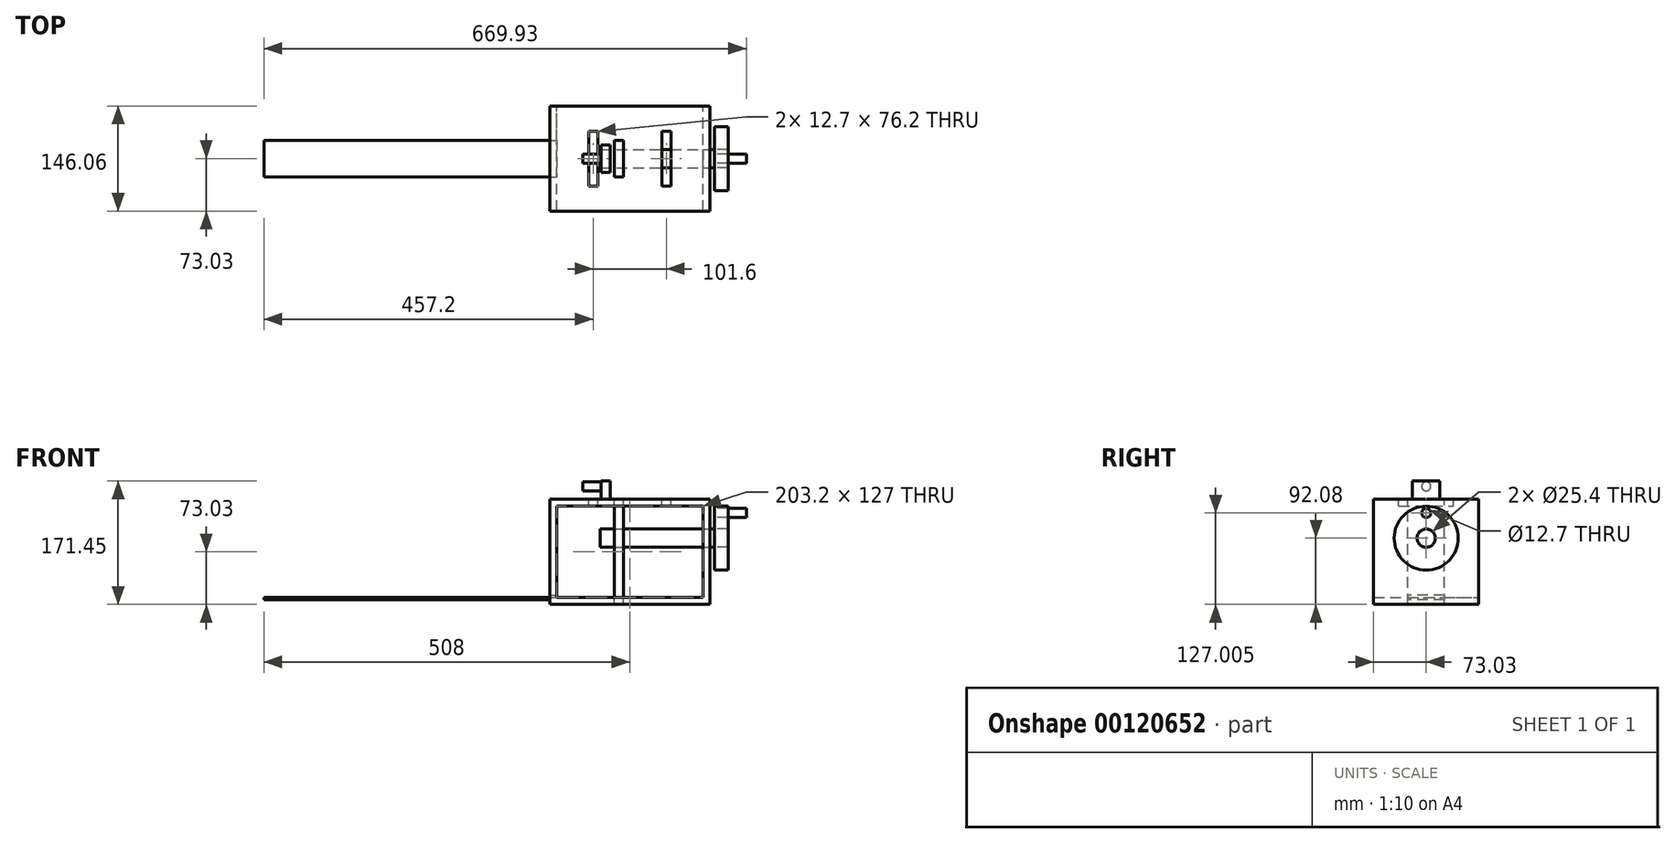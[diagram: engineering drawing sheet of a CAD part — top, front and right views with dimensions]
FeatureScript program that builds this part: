
annotation { "Feature Type Name" : "Feature", "Feature Type Description" : "" }
export const myFeature = defineFeature(function(context is Context, id is Id, definition is map)
    precondition{}
    {
        {
            var Q0;
            Q0=qCreatedBy(makeId("Front.planeOp"),FACE);
            var sketch = newSketch(context, id + "F0", { "sketchPlane" : qUnion([Q0])});
            skLineSegment(sketch, "E0.bottom", {"start": v(101.6, 63.5) * mm, "end": v(-101.6, 63.5) * mm});
            skLineSegment(sketch, "E0.top", {"start": v(101.6, -63.5) * mm, "end": v(-101.6, -63.5) * mm});
            skLineSegment(sketch, "E0.left", {"start": v(101.6, 63.5) * mm, "end": v(101.6, -63.5) * mm});
            skLineSegment(sketch, "E0.right", {"start": v(-101.6, 63.5) * mm, "end": v(-101.6, -63.5) * mm});
            skPoint(sketch, "E0.middle", {"position": v(0, 0) * mm});
            skLineSegment(sketch, "E1.bottom", {"start": v(111.13, 73.03) * mm, "end": v(-111.12, 73.03) * mm});
            skLineSegment(sketch, "E1.top", {"start": v(111.12, -73.02) * mm, "end": v(-111.12, -73.02) * mm});
            skLineSegment(sketch, "E1.left", {"start": v(111.12, 73.03) * mm, "end": v(111.12, -73.03) * mm});
            skLineSegment(sketch, "E1.right", {"start": v(-111.12, 73.03) * mm, "end": v(-111.12, -73.03) * mm});
            skSolve(sketch);
        }
        {
            var Q0;
            Q0 = qSketchRegion(id + "F0", true);
            extrude(context, id + "F1", {"entities" : qUnion([Q0]), "endBound" : BoundingType.SYMMETRIC, "depth" : 146.05 * mm});
        }
        {
            var Q0;
            Q0=makeQuery(id+"F1.opExtrude","SWEPT_FACE",FACE,{"disambiguationData":[OSD([sQuery(id+"F0.wireOp",EDGE,"E0.right")])]});
            var sketch = newSketch(context, id + "F2", { "sketchPlane" : qUnion([Q0])});
            skLineSegment(sketch, "E2.bottom", {"start": v(25.4, -60.32) * mm, "end": v(-25.4, -60.32) * mm});
            skLineSegment(sketch, "E2.top", {"start": v(25.4, -66.67) * mm, "end": v(-25.4, -66.67) * mm});
            skLineSegment(sketch, "E2.left", {"start": v(25.4, -60.32) * mm, "end": v(25.4, -66.67) * mm});
            skLineSegment(sketch, "E2.right", {"start": v(-25.4, -60.32) * mm, "end": v(-25.4, -66.67) * mm});
            skPoint(sketch, "E2.middle", {"position": v(0, -63.5) * mm});
            skSolve(sketch);
        }
        {
            var Q0;
            Q0 = qSketchRegion(id + "F2", true);
            extrude(context, id + "F3", {"entities" : qUnion([Q0]), "operationType" : NewBodyOperationType.REMOVE, "oppositeDirection" : true, "depth" : 25.4 * mm});
        }
        {
            var Q0;
            Q0=makeQuery(id+"F1.opExtrude","SWEPT_FACE",FACE,{"disambiguationData":[OSD([sQuery(id+"F0.wireOp",EDGE,"E1.left")])]});
            var sketch = newSketch(context, id + "F4", { "sketchPlane" : qUnion([Q0])});
            skLineSegment(sketch, "E3", {"start": v(0, 73.03) * mm, "end": v(0, 19.05) * mm, "construction": true});
            skCircle(sketch, "E4", {"center": v(0, 19.05) * mm, "radius": 12.7 * mm});
            skSolve(sketch);
        }
        {
            var Q0;
            Q0 = qSketchRegion(id + "F4", true);
            extrude(context, id + "F5", {"entities" : qUnion([Q0]), "operationType" : NewBodyOperationType.REMOVE, "endBound" : BoundingType.UP_TO_NEXT, "oppositeDirection" : true, "depth" : 25.4 * mm});
        }
        {
            var Q0;
            Q0=makeQuery(id+"F1.opExtrude","SWEPT_FACE",FACE,{"disambiguationData":[OSD([sQuery(id+"F0.wireOp",EDGE,"E1.left")])]});
            var sketch = newSketch(context, id + "F6", { "sketchPlane" : qUnion([Q0])});
            skLineSegment(sketch, "E5", {"start": v(0, 73.03) * mm, "end": v(0, -73.03) * mm, "construction": true});
            skCircle(sketch, "E6.0", {"center": v(0, 19.05) * mm, "radius": 12.7 * mm});
            skSolve(sketch);
        }
        {
            var Q0;
            Q0 = qSketchRegion(id + "F6", true);
            var Q1;
            Q1=sQuery(id+"F6.wireOp",EDGE,"szUsaJbX-46pl-vjBz-fUtL-dvWnpHGhxo7Z");
            extrude(context, id + "F7", {"entities" : qUnion([Q0]), "surfaceEntities" : qUnion([Q1]), "oppositeDirection" : true, "depth" : 152.4 * mm});
        }
        {
            var Q0;
            Q0=makeQuery(id+"F1.opExtrude","SWEPT_FACE",FACE,{"disambiguationData":[OSD([sQuery(id+"F0.wireOp",EDGE,"E1.left")])]});
            var sketch = newSketch(context, id + "F8", { "sketchPlane" : qUnion([Q0])});
            skLineSegment(sketch, "E7", {"start": v(0, 73.03) * mm, "end": v(0, -73.03) * mm, "construction": true});
            skCircle(sketch, "E8", {"center": v(0, 19.05) * mm, "radius": 12.7 * mm});
            skSolve(sketch);
        }
        {
            var Q0;
            Q0=makeQuery(id+"F8.imprint","IMPRINT",FACE,{"disambiguationData":[TD([[makeQuery(id+"F8.imprint","IMPRINT",EDGE,{"derivedFrom":sQuery(id+"F8.wireOp",EDGE,"E8")}),1.0]])]});
            extrude(context, id + "F9", {"entities" : qUnion([Q0]), "depth" : 6.35 * mm});
        }
        {
            var Q0;
            Q0=makeQuery(id+"F9.opExtrude","CAP_FACE",FACE,{"disambiguationData":[OSD([sQuery(id+"F8.wireOp",EDGE,"E8")])],"isStart":false});
            var sketch = newSketch(context, id + "F10", { "sketchPlane" : qUnion([Q0])});
            skCircle(sketch, "E9", {"center": v(0, 19.05) * mm, "radius": 44.45 * mm});
            skCircle(sketch, "E10", {"center": v(0, 53.98) * mm, "radius": 6.35 * mm});
            skCircle(sketch, "E11", {"center": v(0, 19.05) * mm, "radius": 34.93 * mm, "construction": true});
            skCircle(sketch, "E12.0", {"center": v(0, 19.05) * mm, "radius": 12.7 * mm});
            skSolve(sketch);
        }
        {
            var Q0;
            Q0 = qSketchRegion(id + "F10", true);
            extrude(context, id + "F11", {"entities" : qUnion([Q0]), "operationType" : NewBodyOperationType.ADD, "depth" : 19.05 * mm});
        }
        {
            var Q0;
            Q0=makeQuery(id+"F11.opExtrude","CAP_FACE",FACE,{"disambiguationData":[OSD([sQuery(id+"F10.wireOp",EDGE,"E9")])],"isStart":false});
            var sketch = newSketch(context, id + "F12", { "sketchPlane" : qUnion([Q0])});
            skCircle(sketch, "E13.0", {"center": v(0, 53.98) * mm, "radius": 6.35 * mm});
            skSolve(sketch);
        }
        {
            var Q0;
            Q0 = qSketchRegion(id + "F12", true);
            extrude(context, id + "F13", {"entities" : qUnion([Q0]), "operationType" : NewBodyOperationType.ADD, "depth" : 25.4 * mm});
        }
        {
            var Q0;
            Q0=makeQuery(id+"F1.opExtrude","SWEPT_FACE",FACE,{"disambiguationData":[OSD([sQuery(id+"F0.wireOp",EDGE,"E1.bottom")])]});
            var sketch = newSketch(context, id + "F14", { "sketchPlane" : qUnion([Q0])});
            skLineSegment(sketch, "E14", {"start": v(0, 73.03) * mm, "end": v(0, -73.03) * mm, "construction": true});
            skLineSegment(sketch, "E15", {"start": v(-111.12, 0) * mm, "end": v(111.12, 0) * mm, "construction": true});
            skLineSegment(sketch, "E16", {"start": v(-50.8, 73.03) * mm, "end": v(0, 73.03) * mm, "construction": true});
            skLineSegment(sketch, "E17", {"start": v(0, 73.03) * mm, "end": v(50.8, 73.03) * mm, "construction": true});
            skLineSegment(sketch, "E18", {"start": v(-50.8, -73.03) * mm, "end": v(-50.8, 73.03) * mm, "construction": true});
            skLineSegment(sketch, "E19", {"start": v(50.8, 73.03) * mm, "end": v(50.8, -73.03) * mm, "construction": true});
            skLineSegment(sketch, "E20.bottom", {"start": v(-44.45, 38.1) * mm, "end": v(-57.15, 38.1) * mm});
            skLineSegment(sketch, "E20.top", {"start": v(-44.45, -38.1) * mm, "end": v(-57.15, -38.1) * mm});
            skLineSegment(sketch, "E20.left", {"start": v(-44.45, 38.1) * mm, "end": v(-44.45, -38.1) * mm});
            skLineSegment(sketch, "E20.right", {"start": v(-57.15, 38.1) * mm, "end": v(-57.15, -38.1) * mm});
            skPoint(sketch, "E20.middle", {"position": v(-50.8, 0) * mm});
            skLineSegment(sketch, "E21.bottom", {"start": v(57.15, 38.1) * mm, "end": v(44.45, 38.1) * mm});
            skLineSegment(sketch, "E21.top", {"start": v(57.15, -38.1) * mm, "end": v(44.45, -38.1) * mm});
            skLineSegment(sketch, "E21.left", {"start": v(57.15, 38.1) * mm, "end": v(57.15, -38.1) * mm});
            skLineSegment(sketch, "E21.right", {"start": v(44.45, 38.1) * mm, "end": v(44.45, -38.1) * mm});
            skPoint(sketch, "E21.middle", {"position": v(50.8, 0) * mm});
            skSolve(sketch);
        }
        {
            var Q0;
            Q0 = qSketchRegion(id + "F14", true);
            extrude(context, id + "F15", {"entities" : qUnion([Q0]), "operationType" : NewBodyOperationType.REMOVE, "oppositeDirection" : true, "depth" : 19.05 * mm});
        }
        {
            var Q0;
            Q0=makeQuery(id+"F1.opExtrude","SWEPT_FACE",FACE,{"disambiguationData":[OSD([sQuery(id+"F0.wireOp",EDGE,"E1.bottom")])]});
            var sketch = newSketch(context, id + "F16", { "sketchPlane" : qUnion([Q0])});
            skLineSegment(sketch, "E22", {"start": v(-111.12, 0) * mm, "end": v(111.12, 0) * mm, "construction": true});
            skLineSegment(sketch, "E23.bottom", {"start": v(-27.02, 19.05) * mm, "end": v(-39.72, 19.05) * mm});
            skLineSegment(sketch, "E23.top", {"start": v(-27.02, -19.05) * mm, "end": v(-39.72, -19.05) * mm});
            skLineSegment(sketch, "E23.left", {"start": v(-27.02, 19.05) * mm, "end": v(-27.02, -19.05) * mm});
            skLineSegment(sketch, "E23.right", {"start": v(-39.72, 19.05) * mm, "end": v(-39.72, -19.05) * mm});
            skPoint(sketch, "E23.middle", {"position": v(-33.37, 0) * mm});
            skSolve(sketch);
        }
        {
            var Q0;
            Q0=makeQuery(id+"F16.imprint","IMPRINT",FACE,{"disambiguationData":[TD([[makeQuery(id+"F16.imprint","IMPRINT",EDGE,{"derivedFrom":sQuery(id+"F16.wireOp",EDGE,"E23.bottom")}),1.0]])]});
            extrude(context, id + "F17", {"entities" : qUnion([Q0]), "operationType" : NewBodyOperationType.ADD, "depth" : 25.4 * mm});
        }
        {
            var Q0;
            Q0=makeQuery(id+"F17.opExtrude","SWEPT_FACE",FACE,{"disambiguationData":[OSD([sQuery(id+"F16.wireOp",EDGE,"E23.right")])]});
            var sketch = newSketch(context, id + "F18", { "sketchPlane" : qUnion([Q0])});
            skLineSegment(sketch, "E24", {"start": v(0, 98.43) * mm, "end": v(0, 73.03) * mm, "construction": true});
            skLineSegment(sketch, "E25", {"start": v(-19.05, 90.97) * mm, "end": v(19.05, 90.97) * mm, "construction": true});
            skCircle(sketch, "E26", {"center": v(0, 90.97) * mm, "radius": 6.35 * mm});
            skSolve(sketch);
        }
        {
            var Q0;
            Q0=makeQuery(id+"F18.imprint","IMPRINT",FACE,{"disambiguationData":[TD([[makeQuery(id+"F18.imprint","IMPRINT",EDGE,{"derivedFrom":sQuery(id+"F18.wireOp",EDGE,"E26")}),1.0]])]});
            extrude(context, id + "F19", {"entities" : qUnion([Q0]), "operationType" : NewBodyOperationType.ADD, "depth" : 25.4 * mm});
        }
        {
            var Q0;
            {var subQ0=sQuery(id+"F2.wireOp",EDGE,"E2.top");Q0=makeQuery(id+"F2.imprint","IMPRINT",FACE,{"disambiguationData":[TD([[makeQuery(id+"F2.imprint","IMPRINT",EDGE,{"derivedFrom":subQ0}),-1.0]])]});}
            extrude(context, id + "F20", {"entities" : qUnion([Q0]), "operationType" : NewBodyOperationType.ADD, "oppositeDirection" : true, "depth" : 406.4 * mm});
        }
        {
            var Q0;
            Q0=makeQuery(id+"F1.opExtrude","SWEPT_FACE",FACE,{"disambiguationData":[OSD([sQuery(id+"F0.wireOp",EDGE,"E1.bottom")])]});
            var sketch = newSketch(context, id + "F21", { "sketchPlane" : qUnion([Q0])});
            skLineSegment(sketch, "E27", {"start": v(-111.12, 0) * mm, "end": v(111.12, 0) * mm, "construction": true});
            skLineSegment(sketch, "E28", {"start": v(-14.96, 73.03) * mm, "end": v(-14.96, -73.03) * mm, "construction": true});
            skLineSegment(sketch, "E29.bottom", {"start": v(-8.61, 25.4) * mm, "end": v(-21.31, 25.4) * mm});
            skLineSegment(sketch, "E29.top", {"start": v(-8.61, -25.4) * mm, "end": v(-21.31, -25.4) * mm});
            skLineSegment(sketch, "E29.left", {"start": v(-8.61, 25.4) * mm, "end": v(-8.61, -25.4) * mm});
            skLineSegment(sketch, "E29.right", {"start": v(-21.31, 25.4) * mm, "end": v(-21.31, -25.4) * mm});
            skPoint(sketch, "E29.middle", {"position": v(-14.96, 0) * mm});
            skSolve(sketch);
        }
        {
            var Q0;
            Q0=makeQuery(id+"F21.imprint","IMPRINT",FACE,{"disambiguationData":[TD([[makeQuery(id+"F21.imprint","IMPRINT",EDGE,{"derivedFrom":sQuery(id+"F21.wireOp",EDGE,"E29.bottom")}),1.0]])]});
            extrude(context, id + "F22", {"entities" : qUnion([Q0]), "oppositeDirection" : true, "depth" : 146.05 * mm});
        }
    });
